# Revit family: Mini Módulo de Entrada Endereçável Sirius MME-D ILUMAC
name_source: partatom
category: Dispositivos de alarme de incêndio
units: mm (PartAtom-declared; Revit-internal decimal feet)

## family parameters
Com base no plano de trabalho = Não
Compartilhado = Não
Corte com vazios quando carregada = Não
Cota do conector redondo = Utilizar diâmetro
Manter orientação da anotação = Não
Número OmniClass = 23.80.30.11.17
Ponto de cálculo do ambiente = Não
Sempre na vertical = Sim
Tipo de parte = Normal
Título OmniClass = Distribution Boards and Control Panels

## types (1)
- MME-D
    Correntes de consumo = 300uA @ 24Vcc – Em supervisão
1,2mA @ 24Vcc – em alarme.
34mA @ 24Vcc - alarme
    Código = 004059
    Descrição = Mini Módulo de Entrada Endereçável Sirius MME-D
    Dimensões (AxLxP) = 54x35x18mm
    Elevação padrão = 0 mm  [stored 0 ft]
    Endereços programáveis = 1 à 125 (por laço)
    Fabricante = ILUMAC
    Fixação = Caixa de sobrepor com bornes de conexão
    Grau de proteção = IP40
    Impedância do drive de comunicação = 75/100K Ohms (Tx/Rx)
    Material da caixa = Caixa plástica ABS cinza.
    Modelo = MME-D
    Normas técnicas aplicáveis = NBR 17240 | ISO 7240-18
    Peso = 23g
    Protocolo de comunicação = ALF-1000-2 (proprietário)
    Quantidade de dispositivo na entrada = 1 dispositivo (limitados à corrente de 2mA)*
    Temperatura de operação = -55 à 55oC
    Tensão de operação = 18 à 30Vcc
    Tensão nominal = 24Vcc
    Tipo de entrada = 1 zona contato-seco
    Umidade relativa = 0 à 95% (sem condensação)

note: [stored X ft] marks values corroborated as IEEE doubles in the binary element streams (Revit-internal decimal feet)
